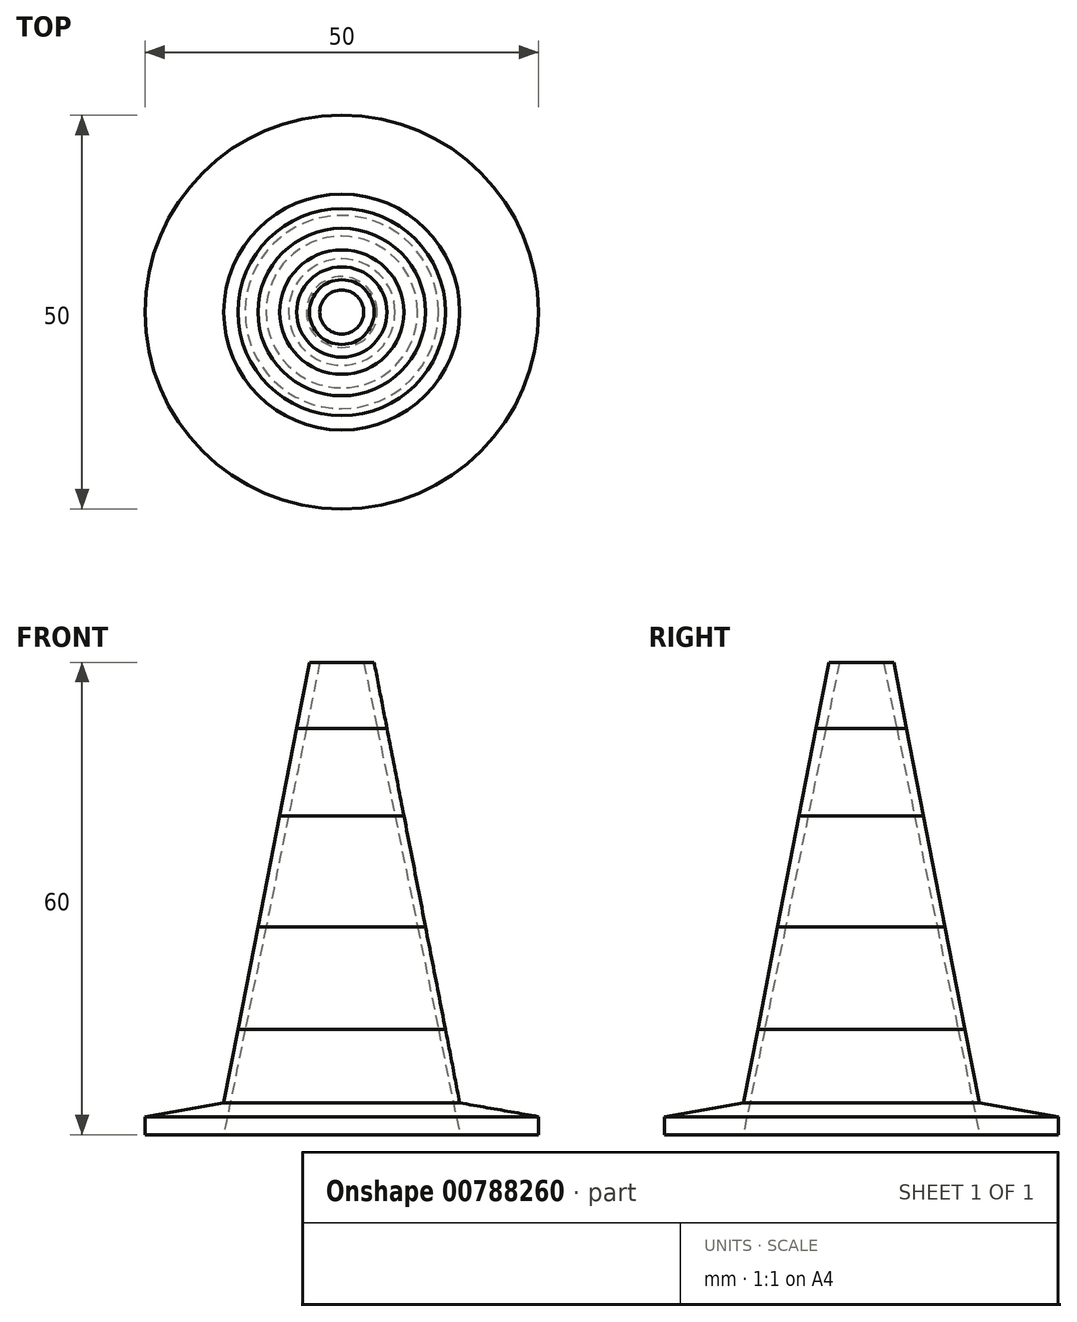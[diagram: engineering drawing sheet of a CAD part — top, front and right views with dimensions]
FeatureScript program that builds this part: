
annotation { "Feature Type Name" : "Feature", "Feature Type Description" : "" }
export const myFeature = defineFeature(function(context is Context, id is Id, definition is map)
    precondition{}
    {
        {
            var Q0;
            Q0=qCreatedBy(makeId("Front.planeOp"),FACE);
            var sketch = newSketch(context, id + "F0", { "sketchPlane" : qUnion([Q0])});
            skLineSegment(sketch, "E0", {"start": v(0, 0) * mm, "end": v(-25, 0) * mm});
            skLineSegment(sketch, "E1", {"start": v(-25, 0) * mm, "end": v(-25, 2.28) * mm});
            skLineSegment(sketch, "E2", {"start": v(-25, 2.28) * mm, "end": v(-14.98, 4.05) * mm});
            skLineSegment(sketch, "E3", {"start": v(-14.98, 4.05) * mm, "end": v(-4.1, 60) * mm});
            skLineSegment(sketch, "E4", {"start": v(-4.1, 60) * mm, "end": v(0, 60) * mm});
            skLineSegment(sketch, "E5", {"start": v(-13.17, 13.4) * mm, "end": v(0, 13.4) * mm});
            skLineSegment(sketch, "E6", {"start": v(-10.64, 26.4) * mm, "end": v(0, 26.4) * mm});
            skLineSegment(sketch, "E7", {"start": v(-7.9, 40.5) * mm, "end": v(0, 40.5) * mm});
            skLineSegment(sketch, "E8", {"start": v(-5.74, 51.6) * mm, "end": v(0, 51.6) * mm});
            skLineSegment(sketch, "E9", {"start": v(0, 60) * mm, "end": v(0, 0) * mm});
            skSolve(sketch);
        }
        {
            var Q0;
            {var subQ0=sQuery(id+"F0.wireOp",EDGE,"E4");Q0=makeQuery(id+"F0.imprint","IMPRINT",FACE,{"disambiguationData":[TD([[makeQuery(id+"F0.imprint","IMPRINT",EDGE,{"derivedFrom":subQ0}),-1.0]])]});}
            var Q1;
            Q1=sQuery(id+"F0.wireOp",EDGE,"E9");
            revolve(context, id + "F1", {"surfaceOperationType" : NewSurfaceOperationType.NEW, "entities" : qUnion([Q0]), "axis" : qUnion([Q1]), "revolveType" : RevolveType.FULL});
        }
        {
            var Q0;
            {var subQ0=sQuery(id+"F0.wireOp",EDGE,"E7");Q0=makeQuery(id+"F0.imprint","IMPRINT",FACE,{"disambiguationData":[TD([[makeQuery(id+"F0.imprint","IMPRINT",EDGE,{"derivedFrom":subQ0}),1.0]])]});}
            var Q1;
            Q1=sQuery(id+"F0.wireOp",EDGE,"E9");
            revolve(context, id + "F2", {"surfaceOperationType" : NewSurfaceOperationType.NEW, "entities" : qUnion([Q0]), "axis" : qUnion([Q1]), "revolveType" : RevolveType.FULL});
        }
        {
            var Q0;
            {var subQ0=sQuery(id+"F0.wireOp",EDGE,"E6");Q0=makeQuery(id+"F0.imprint","IMPRINT",FACE,{"disambiguationData":[TD([[makeQuery(id+"F0.imprint","IMPRINT",EDGE,{"derivedFrom":subQ0}),1.0]])]});}
            var Q1;
            Q1=sQuery(id+"F0.wireOp",EDGE,"E9");
            revolve(context, id + "F3", {"surfaceOperationType" : NewSurfaceOperationType.NEW, "entities" : qUnion([Q0]), "axis" : qUnion([Q1]), "revolveType" : RevolveType.FULL});
        }
        {
            var Q0;
            {var subQ0=sQuery(id+"F0.wireOp",EDGE,"E5");Q0=makeQuery(id+"F0.imprint","IMPRINT",FACE,{"disambiguationData":[TD([[makeQuery(id+"F0.imprint","IMPRINT",EDGE,{"derivedFrom":subQ0}),1.0]])]});}
            var Q1;
            Q1=sQuery(id+"F0.wireOp",EDGE,"E9");
            revolve(context, id + "F4", {"surfaceOperationType" : NewSurfaceOperationType.NEW, "entities" : qUnion([Q0]), "axis" : qUnion([Q1]), "revolveType" : RevolveType.FULL});
        }
        {
            var Q0;
            {var subQ3=sQuery(id+"F0.wireOp",EDGE,"E0");Q0=makeQuery(id+"F0.imprint","IMPRINT",FACE,{"disambiguationData":[TD([[makeQuery(id+"F0.imprint","IMPRINT",EDGE,{"derivedFrom":subQ3}),-1.0]])]});}
            var Q1;
            Q1=sQuery(id+"F0.wireOp",EDGE,"E9");
            revolve(context, id + "F5", {"surfaceOperationType" : NewSurfaceOperationType.NEW, "entities" : qUnion([Q0]), "axis" : qUnion([Q1]), "revolveType" : RevolveType.FULL});
        }
        {
            var Q0;
            Q0=makeQuery(id+"F5.opRevolve","SWEPT_FACE",FACE,{"disambiguationData":[OSD([sQuery(id+"F0.wireOp",EDGE,"E0")])]});
            var sketch = newSketch(context, id + "F6", { "sketchPlane" : qUnion([Q0])});
            skCircle(sketch, "E10", {"center": v(0, 0) * mm, "radius": 15 * mm});
            skSolve(sketch);
        }
        {
            var Q0;
            Q0=makeQuery(id+"F6.imprint","IMPRINT",FACE,{"disambiguationData":[TD([[makeQuery(id+"F6.imprint","IMPRINT",EDGE,{"derivedFrom":sQuery(id+"F6.wireOp",EDGE,"E10")}),1.0]])]});
            extrude(context, id + "F7", {"entities" : qUnion([Q0]), "operationType" : NewBodyOperationType.REMOVE, "oppositeDirection" : true, "depth" : 70.4 * mm, "offsetDistance" : 25 * mm, "hasDraft" : true, "draftAngle" : 11.5 * degree, "draftPullDirection" : true});
        }
    });
